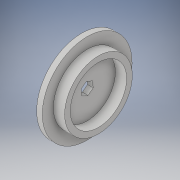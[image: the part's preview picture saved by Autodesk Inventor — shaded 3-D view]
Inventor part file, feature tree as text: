
AUTODESK INVENTOR PART (.ipt)
format: ipt  version: 2018 (Build 220112000, 112)  size: 126,976 bytes
history: native  units: in
note: dims shown in document units (in); Inventor stores cm internally (conversion verified against a paired STEP export)
features: extrude x3, sketch x3
ambient origin geometry x8: Origin, YZ Plane, XZ Plane, XY Plane, X Axis, Y Axis, Z Axis, Center Point
bodies: Solid1 (feature_tree)
feature tree (6):
  extrude  "Extrusion1"  Depth=0.25in TaperAngle=0.0deg
  extrude  "Extrusion2"  Depth=0.25in
  extrude  "Extrusion3"  Depth=0.5in
  sketch  "Sketch1"  dims[d0=3.98in d1=0.25in d2=0.0in]
  sketch  "Sketch2"  dims[d3=3.0in d4=0.25in]
  sketch  "Sketch3"  dims[d5=0.5in d6=0.0in d7=0.5in d8=0.5in d9=0.0in]
